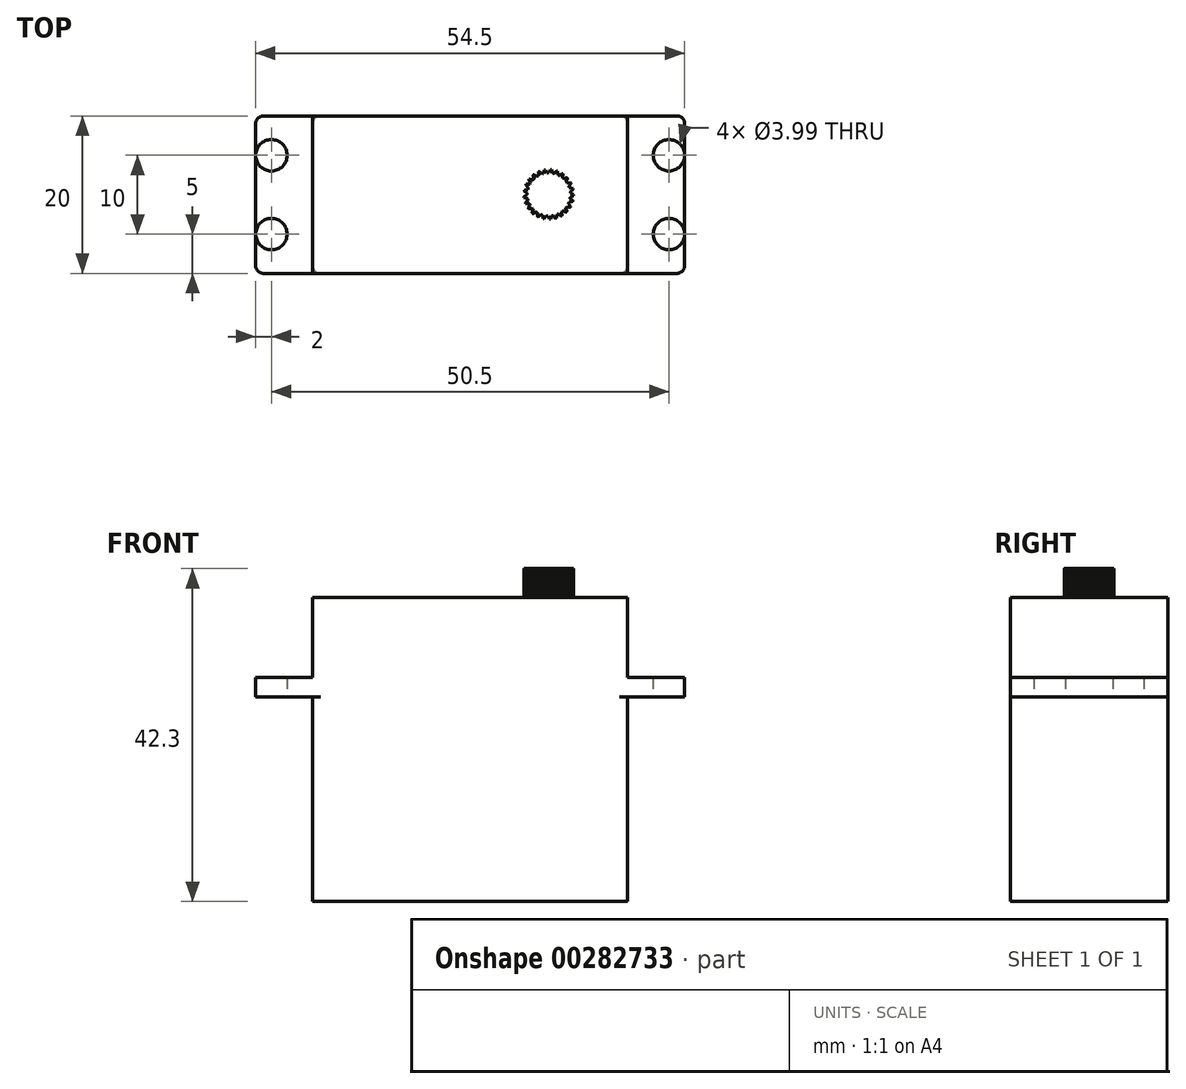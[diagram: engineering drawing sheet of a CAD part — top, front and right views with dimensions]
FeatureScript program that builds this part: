
annotation { "Feature Type Name" : "Feature", "Feature Type Description" : "" }
export const myFeature = defineFeature(function(context is Context, id is Id, definition is map)
    precondition{}
    {
        {
            var Q0;
            Q0=qCreatedBy(makeId("Top.planeOp"),FACE);
            var sketch = newSketch(context, id + "F0", { "sketchPlane" : qUnion([Q0])});
            skLineSegment(sketch, "E0", {"start": v(-74.17, 0) * mm, "end": v(76.51, 0) * mm, "construction": true});
            skLineSegment(sketch, "E1", {"start": v(0, 74.75) * mm, "end": v(0, -75.53) * mm, "construction": true});
            skLineSegment(sketch, "E2.bottom", {"start": v(19, -10) * mm, "end": v(-19, -10) * mm});
            skLineSegment(sketch, "E2.top", {"start": v(19, 10) * mm, "end": v(-19, 10) * mm});
            skLineSegment(sketch, "E2.left", {"start": v(20, -9) * mm, "end": v(20, 9) * mm});
            skLineSegment(sketch, "E2.right", {"start": v(-20, -9) * mm, "end": v(-20, 9) * mm});
            skPoint(sketch, "E2.middle", {"position": v(0, 0) * mm});
            skPoint(sketch, "E3.visualSharp", {"position": v(-20, 10) * mm});
            skArc(sketch, "E3.filletArc", {"start": v(-19, 10) * mm, "mid": v(-19.7, 9.7) * mm, "end": v(-20, 9) * mm});
            skPoint(sketch, "E4.visualSharp", {"position": v(20, 10) * mm});
            skArc(sketch, "E4.filletArc", {"start": v(20, 9) * mm, "mid": v(19.7, 9.7) * mm, "end": v(19, 10) * mm});
            skPoint(sketch, "E5.visualSharp", {"position": v(20, -10) * mm});
            skArc(sketch, "E5.filletArc", {"start": v(19, -10) * mm, "mid": v(19.7, -9.7) * mm, "end": v(20, -9) * mm});
            skPoint(sketch, "E6.visualSharp", {"position": v(-20, -10) * mm});
            skArc(sketch, "E6.filletArc", {"start": v(-20, -9) * mm, "mid": v(-19.7, -9.7) * mm, "end": v(-19, -10) * mm});
            skSolve(sketch);
        }
        {
            var Q0;
            Q0 = qSketchRegion(id + "F0", true);
            extrude(context, id + "F1", {"entities" : qUnion([Q0]), "depth" : 26 * mm});
        }
        {
            var Q0;
            Q0=makeQuery(id+"F1.opExtrude","CAP_FACE",FACE,{"disambiguationData":[OSD([sQuery(id+"F0.wireOp",EDGE,"E2.bottom"),sQuery(id+"F0.wireOp",EDGE,"E2.top"),sQuery(id+"F0.wireOp",EDGE,"E2.left"),sQuery(id+"F0.wireOp",EDGE,"E2.right"),sQuery(id+"F0.wireOp",EDGE,"E3.filletArc"),sQuery(id+"F0.wireOp",EDGE,"E4.filletArc"),sQuery(id+"F0.wireOp",EDGE,"E5.filletArc"),sQuery(id+"F0.wireOp",EDGE,"E6.filletArc")])],"isStart":false});
            var sketch = newSketch(context, id + "F2", { "sketchPlane" : qUnion([Q0])});
            skLineSegment(sketch, "E7", {"start": v(-69.92, 0) * mm, "end": v(54, 0) * mm, "construction": true});
            skPoint(sketch, "E7.startSnap0", {"position": v(-20, 0) * mm});
            skLineSegment(sketch, "E8", {"start": v(0, 31.92) * mm, "end": v(0, -23.22) * mm, "construction": true});
            skLineSegment(sketch, "E9.bottom", {"start": v(26.25, -10) * mm, "end": v(-26.25, -10) * mm});
            skLineSegment(sketch, "E9.top", {"start": v(26.25, 10) * mm, "end": v(-26.25, 10) * mm});
            skLineSegment(sketch, "E9.left", {"start": v(27.25, -9) * mm, "end": v(27.25, 9) * mm});
            skLineSegment(sketch, "E9.right", {"start": v(-27.25, -9) * mm, "end": v(-27.25, 9) * mm});
            skPoint(sketch, "E9.middle", {"position": v(0, 0) * mm});
            skLineSegment(sketch, "E10", {"start": v(-25.25, 12.88) * mm, "end": v(-25.25, -17.15) * mm, "construction": true});
            skPoint(sketch, "E11", {"position": v(-25.25, 5) * mm});
            skPoint(sketch, "E12", {"position": v(-25.25, -5) * mm});
            skPoint(sketch, "E13.MirrorP", {"position": v(25.25, 5) * mm});
            skPoint(sketch, "E14.MirrorP", {"position": v(25.25, -5) * mm});
            skPoint(sketch, "E15.visualSharp", {"position": v(-27.25, 10) * mm});
            skArc(sketch, "E15.filletArc", {"start": v(-26.25, 10) * mm, "mid": v(-26.96, 9.7) * mm, "end": v(-27.25, 9) * mm});
            skPoint(sketch, "E16.visualSharp", {"position": v(-27.25, -10) * mm});
            skArc(sketch, "E16.filletArc", {"start": v(-27.25, -9) * mm, "mid": v(-26.96, -9.7) * mm, "end": v(-26.25, -10) * mm});
            skPoint(sketch, "E17.visualSharp", {"position": v(27.25, 10) * mm});
            skArc(sketch, "E17.filletArc", {"start": v(27.25, 9) * mm, "mid": v(26.96, 9.7) * mm, "end": v(26.25, 10) * mm});
            skPoint(sketch, "E18.visualSharp", {"position": v(27.25, -10) * mm});
            skArc(sketch, "E18.filletArc", {"start": v(26.25, -10) * mm, "mid": v(26.96, -9.7) * mm, "end": v(27.25, -9) * mm});
            skSolve(sketch);
        }
        {
            var Q0;
            Q0 = qSketchRegion(id + "F2", true);
            extrude(context, id + "F3", {"entities" : qUnion([Q0]), "operationType" : NewBodyOperationType.ADD, "depth" : 2.5 * mm});
        }
        {
            var Q0;
            Q0=sQuery(id+"F2.wireOp",VERTEX,"E11");
            var Q1;
            Q1=sQuery(id+"F2.wireOp",VERTEX,"E12");
            var Q2;
            Q2=sQuery(id+"F2.wireOp",VERTEX,"E13.MirrorP");
            var Q3;
            Q3=sQuery(id+"F2.wireOp",VERTEX,"E14.MirrorP");
            var Q4;
            Q4=makeQuery(id+"F1.opExtrude","SWEPT_BODY",BODY,{"disambiguationData":[OSD([sQuery(id+"F0.wireOp",EDGE,"E2.bottom"),sQuery(id+"F0.wireOp",EDGE,"E2.top"),sQuery(id+"F0.wireOp",EDGE,"E2.left"),sQuery(id+"F0.wireOp",EDGE,"E2.right"),sQuery(id+"F0.wireOp",EDGE,"E3.filletArc"),sQuery(id+"F0.wireOp",EDGE,"E4.filletArc"),sQuery(id+"F0.wireOp",EDGE,"E5.filletArc"),sQuery(id+"F0.wireOp",EDGE,"E6.filletArc")])]});
            hole(context, id + "F4", {"style" : HoleStyle.SIMPLE, "endStyle" : HoleEndStyle.BLIND, "oppositeDirection" : true, "holeDiameter" : 4 * mm, "holeDepth" : 5 * mm, "tappedDepth" : 12 * mm, "tapClearance" : 3, "startFromSketch" : true, "locations" : qUnion([Q0, Q1, Q2, Q3]), "scope" : qUnion([Q4])});
        }
        {
            var Q0;
            Q0=makeQuery(id+"F3.opExtrude","CAP_FACE",FACE,{"disambiguationData":[OSD([sQuery(id+"F2.wireOp",EDGE,"E9.bottom"),sQuery(id+"F2.wireOp",EDGE,"E9.top"),sQuery(id+"F2.wireOp",EDGE,"E9.left"),sQuery(id+"F2.wireOp",EDGE,"E9.right"),sQuery(id+"F2.wireOp",EDGE,"E15.filletArc"),sQuery(id+"F2.wireOp",EDGE,"E16.filletArc"),sQuery(id+"F2.wireOp",EDGE,"E17.filletArc"),sQuery(id+"F2.wireOp",EDGE,"E18.filletArc")])],"isStart":false});
            var sketch = newSketch(context, id + "F5", { "sketchPlane" : qUnion([Q0])});
            skLineSegment(sketch, "E19.bottom", {"start": v(20, -10) * mm, "end": v(-20, -10) * mm});
            skLineSegment(sketch, "E19.top", {"start": v(20, 10) * mm, "end": v(-20, 10) * mm});
            skLineSegment(sketch, "E19.left", {"start": v(20, -10) * mm, "end": v(20, 10) * mm});
            skLineSegment(sketch, "E19.right", {"start": v(-20, -10) * mm, "end": v(-20, 10) * mm});
            skPoint(sketch, "E19.middle", {"position": v(0, 0) * mm});
            skSolve(sketch);
        }
        {
            var Q0;
            Q0 = qSketchRegion(id + "F5", true);
            extrude(context, id + "F6", {"entities" : qUnion([Q0]), "operationType" : NewBodyOperationType.ADD, "depth" : 10.1 * mm});
        }
        {
            var Q0;
            Q0=makeQuery(id+"F6.opExtrude","CAP_FACE",FACE,{"disambiguationData":[OSD([sQuery(id+"F5.wireOp",EDGE,"E19.bottom"),sQuery(id+"F5.wireOp",EDGE,"E19.top"),sQuery(id+"F5.wireOp",EDGE,"E19.left"),sQuery(id+"F5.wireOp",EDGE,"E19.right")])],"isStart":false});
            var sketch = newSketch(context, id + "F7", { "sketchPlane" : qUnion([Q0])});
            skLineSegment(sketch, "E20", {"start": v(-27.08, 0) * mm, "end": v(27.57, 0) * mm, "construction": true});
            skPoint(sketch, "E20.startSnap0", {"position": v(-20, 0) * mm});
            skPoint(sketch, "E20.endSnap0", {"position": v(20, 0) * mm});
            skLineSegment(sketch, "E21", {"start": v(0, 10) * mm, "end": v(0, -10) * mm, "construction": true});
            skLineSegment(sketch, "E22", {"start": v(10, 10) * mm, "end": v(10, -10) * mm, "construction": true});
            skPoint(sketch, "E23", {"position": v(10, 0) * mm});
            skCircle(sketch, "E24", {"center": v(10, 0) * mm, "radius": 2.5 * mm});
            skLineSegment(sketch, "E25", {"start": v(30, 0.07) * mm, "end": v(30, -0.07) * mm});
            skLineSegment(sketch, "E26", {"start": v(28.57, 1.57) * mm, "end": v(13.29, 2.34) * mm});
            skLineSegment(sketch, "E27", {"start": v(28.58, -1.57) * mm, "end": v(13.28, -2.34) * mm});
            skPoint(sketch, "E28.visualSharp", {"position": v(30, 1.5) * mm});
            skArc(sketch, "E28.filletArc", {"start": v(30, 0.07) * mm, "mid": v(29.59, 1.1) * mm, "end": v(28.57, 1.57) * mm});
            skPoint(sketch, "E29.visualSharp", {"position": v(30, -1.5) * mm});
            skArc(sketch, "E29.filletArc", {"start": v(28.58, -1.57) * mm, "mid": v(29.59, -1.1) * mm, "end": v(30, -0.07) * mm});
            skLineSegment(sketch, "E30.1.0", {"start": v(8.43, 18.57) * mm, "end": v(7.66, 3.29) * mm});
            skPoint(sketch, "E30.1.1", {"position": v(8.5, 20) * mm});
            skArc(sketch, "E30.1.2", {"start": v(9.93, 20) * mm, "mid": v(8.9, 19.59) * mm, "end": v(8.43, 18.57) * mm});
            skArc(sketch, "E30.1.3", {"start": v(11.57, 18.58) * mm, "mid": v(11.1, 19.59) * mm, "end": v(10.07, 20) * mm});
            skLineSegment(sketch, "E30.1.4", {"start": v(11.57, 18.58) * mm, "end": v(12.34, 3.28) * mm});
            skLineSegment(sketch, "E30.2.0", {"start": v(-8.57, -1.57) * mm, "end": v(6.71, -2.34) * mm});
            skPoint(sketch, "E30.2.1", {"position": v(-10, -1.5) * mm});
            skArc(sketch, "E30.2.2", {"start": v(-10, -0.07) * mm, "mid": v(-9.59, -1.1) * mm, "end": v(-8.57, -1.57) * mm});
            skArc(sketch, "E30.2.3", {"start": v(-8.58, 1.57) * mm, "mid": v(-9.59, 1.1) * mm, "end": v(-10, 0.07) * mm});
            skLineSegment(sketch, "E30.2.4", {"start": v(-8.58, 1.57) * mm, "end": v(6.72, 2.34) * mm});
            skLineSegment(sketch, "E30.3.0", {"start": v(11.57, -18.57) * mm, "end": v(12.34, -3.29) * mm});
            skPoint(sketch, "E30.3.1", {"position": v(11.5, -20) * mm});
            skArc(sketch, "E30.3.2", {"start": v(10.07, -20) * mm, "mid": v(11.1, -19.59) * mm, "end": v(11.57, -18.57) * mm});
            skArc(sketch, "E30.3.3", {"start": v(8.43, -18.58) * mm, "mid": v(8.9, -19.59) * mm, "end": v(9.93, -20) * mm});
            skLineSegment(sketch, "E30.3.4", {"start": v(8.43, -18.58) * mm, "end": v(7.66, -3.28) * mm});
            skPoint(sketch, "E31.newPointA", {"position": v(12.5, 0.13) * mm});
            skPoint(sketch, "E31.newPointB", {"position": v(10, 2.5) * mm});
            skArc(sketch, "E31.filletArc", {"start": v(12.34, 3.28) * mm, "mid": v(12.63, 2.63) * mm, "end": v(13.29, 2.34) * mm});
            skPoint(sketch, "E32.newPointA", {"position": v(12.5, 0) * mm});
            skPoint(sketch, "E32.newPointB", {"position": v(10.13, -2.5) * mm});
            skArc(sketch, "E32.filletArc", {"start": v(13.28, -2.34) * mm, "mid": v(12.63, -2.63) * mm, "end": v(12.34, -3.29) * mm});
            skPoint(sketch, "E33.newPointA", {"position": v(10, -2.5) * mm});
            skPoint(sketch, "E33.newPointB", {"position": v(7.5, -0.13) * mm});
            skArc(sketch, "E33.filletArc", {"start": v(7.66, -3.28) * mm, "mid": v(7.37, -2.63) * mm, "end": v(6.71, -2.34) * mm});
            skPoint(sketch, "E34.newPointA", {"position": v(9.87, 2.5) * mm});
            skPoint(sketch, "E34.newPointB", {"position": v(7.5, 0) * mm});
            skArc(sketch, "E34.filletArc", {"start": v(6.72, 2.34) * mm, "mid": v(7.37, 2.63) * mm, "end": v(7.66, 3.29) * mm});
            skSolve(sketch);
        }
        {
            var Q0;
            Q0 = qSketchRegion(id + "F7", true);
            extrude(context, id + "F8", {"entities" : qUnion([Q0]), "depth" : 6 * mm});
        }
        {
            var Q0;
            Q0=makeQuery(id+"F8.opExtrude","CAP_FACE",FACE,{"disambiguationData":[OSD([sQuery(id+"F7.wireOp",EDGE,"E24")])],"isStart":false});
            var sketch = newSketch(context, id + "F9", { "sketchPlane" : qUnion([Q0])});
            skLineSegment(sketch, "E35", {"start": v(-26.82, 0) * mm, "end": v(26.9, 0) * mm, "construction": true});
            skLineSegment(sketch, "E36", {"start": v(10, 9.8) * mm, "end": v(10, -10.05) * mm, "construction": true});
            skCircle(sketch, "E37", {"center": v(10, 0) * mm, "radius": 2.5 * mm, "construction": true});
            skLineSegment(sketch, "E38", {"start": v(-7, 0.09) * mm, "end": v(-7, -0.09) * mm});
            skLineSegment(sketch, "E39", {"start": v(-5.59, 1.58) * mm, "end": v(4.98, 2.2) * mm});
            skLineSegment(sketch, "E40", {"start": v(-5.59, -1.58) * mm, "end": v(4.97, -2.2) * mm});
            skPoint(sketch, "E41.visualSharp", {"position": v(-7, 1.5) * mm});
            skArc(sketch, "E41.filletArc", {"start": v(-5.59, 1.58) * mm, "mid": v(-6.6, 1.11) * mm, "end": v(-7, 0.09) * mm});
            skPoint(sketch, "E42.visualSharp", {"position": v(-7, -1.5) * mm});
            skArc(sketch, "E42.filletArc", {"start": v(-7, -0.09) * mm, "mid": v(-6.6, -1.11) * mm, "end": v(-5.59, -1.58) * mm});
            skLineSegment(sketch, "E43.1.0", {"start": v(8.42, -15.59) * mm, "end": v(7.8, -5.02) * mm});
            skArc(sketch, "E43.1.1", {"start": v(8.42, -15.59) * mm, "mid": v(8.89, -16.6) * mm, "end": v(9.91, -17) * mm});
            skArc(sketch, "E43.1.2", {"start": v(10.09, -17) * mm, "mid": v(11.11, -16.6) * mm, "end": v(11.58, -15.59) * mm});
            skLineSegment(sketch, "E43.1.3", {"start": v(11.58, -15.59) * mm, "end": v(12.2, -5.03) * mm});
            skLineSegment(sketch, "E43.1.4", {"start": v(9.91, -17) * mm, "end": v(10.09, -17) * mm});
            skLineSegment(sketch, "E43.2.0", {"start": v(25.59, -1.58) * mm, "end": v(15.02, -2.2) * mm});
            skArc(sketch, "E43.2.1", {"start": v(25.59, -1.58) * mm, "mid": v(26.6, -1.11) * mm, "end": v(27, -0.09) * mm});
            skArc(sketch, "E43.2.2", {"start": v(27, 0.09) * mm, "mid": v(26.6, 1.11) * mm, "end": v(25.59, 1.58) * mm});
            skLineSegment(sketch, "E43.2.3", {"start": v(25.59, 1.58) * mm, "end": v(15.03, 2.2) * mm});
            skLineSegment(sketch, "E43.2.4", {"start": v(27, -0.09) * mm, "end": v(27, 0.09) * mm});
            skLineSegment(sketch, "E43.3.0", {"start": v(11.58, 15.59) * mm, "end": v(12.2, 5.02) * mm});
            skArc(sketch, "E43.3.1", {"start": v(11.58, 15.59) * mm, "mid": v(11.11, 16.6) * mm, "end": v(10.09, 17) * mm});
            skArc(sketch, "E43.3.2", {"start": v(9.91, 17) * mm, "mid": v(8.89, 16.6) * mm, "end": v(8.42, 15.59) * mm});
            skLineSegment(sketch, "E43.3.3", {"start": v(8.42, 15.59) * mm, "end": v(7.8, 5.03) * mm});
            skLineSegment(sketch, "E43.3.4", {"start": v(10.09, 17) * mm, "end": v(9.91, 17) * mm});
            skPoint(sketch, "E44.newPointA", {"position": v(9.85, 2.5) * mm});
            skPoint(sketch, "E44.newPointB", {"position": v(7.5, 0) * mm});
            skArc(sketch, "E44.filletArc", {"start": v(4.98, 2.2) * mm, "mid": v(6.92, 3.08) * mm, "end": v(7.8, 5.03) * mm});
            skPoint(sketch, "E45.newPointA", {"position": v(12.5, 0.15) * mm});
            skPoint(sketch, "E45.newPointB", {"position": v(10, 2.5) * mm});
            skArc(sketch, "E45.filletArc", {"start": v(12.2, 5.02) * mm, "mid": v(13.08, 3.08) * mm, "end": v(15.03, 2.2) * mm});
            skPoint(sketch, "E46.newPointA", {"position": v(10.15, -2.5) * mm});
            skPoint(sketch, "E46.newPointB", {"position": v(12.5, 0) * mm});
            skArc(sketch, "E46.filletArc", {"start": v(15.02, -2.2) * mm, "mid": v(13.08, -3.08) * mm, "end": v(12.2, -5.03) * mm});
            skPoint(sketch, "E47.newPointA", {"position": v(10, -2.5) * mm});
            skPoint(sketch, "E47.newPointB", {"position": v(7.5, -0.15) * mm});
            skArc(sketch, "E47.filletArc", {"start": v(7.8, -5.02) * mm, "mid": v(6.92, -3.08) * mm, "end": v(4.97, -2.2) * mm});
            skSolve(sketch);
        }
        {
            var Q0;
            Q0 = qSketchRegion(id + "F9", true);
            extrude(context, id + "F10", {"entities" : qUnion([Q0]), "operationType" : NewBodyOperationType.ADD, "depth" : 2 * mm});
        }
        {
            var Q0;
            Q0=makeQuery(id+"F8.opExtrude","SWEPT_BODY",BODY,{"disambiguationData":[OSD([sQuery(id+"F7.wireOp",EDGE,"E24")])]});
            deleteBodies(context, id + "F11", {"entities" : qUnion([Q0])});
        }
        {
            var Q0;
            Q0=makeQuery(id+"F6.opExtrude","CAP_FACE",FACE,{"disambiguationData":[OSD([sQuery(id+"F5.wireOp",EDGE,"E19.bottom"),sQuery(id+"F5.wireOp",EDGE,"E19.top"),sQuery(id+"F5.wireOp",EDGE,"E19.left"),sQuery(id+"F5.wireOp",EDGE,"E19.right")])],"isStart":false});
            var sketch = newSketch(context, id + "F12", { "sketchPlane" : qUnion([Q0])});
            skLineSegment(sketch, "E48", {"start": v(-32.03, 0) * mm, "end": v(35.55, 0) * mm, "construction": true});
            skPoint(sketch, "E48.startSnap0", {"position": v(-20, 0) * mm});
            skPoint(sketch, "E48.endSnap0", {"position": v(20, 0) * mm});
            skLineSegment(sketch, "E49", {"start": v(10, 15) * mm, "end": v(10, -15) * mm, "construction": true});
            skPoint(sketch, "E50", {"position": v(10, 0) * mm});
            skCircle(sketch, "E51", {"center": v(10, 0.03) * mm, "radius": 2.75 * mm, "construction": true});
            skArc(sketch, "E52", {"start": v(10.2, 3.17) * mm, "mid": v(9.72, -3.11) * mm, "end": v(10.34, 3.16) * mm, "construction": true});
            skLineSegment(sketch, "E53", {"start": v(10, 0.03) * mm, "end": v(10.82, 3.22) * mm, "construction": true});
            skLineSegment(sketch, "E54", {"start": v(10, 0.03) * mm, "end": v(10.57, 3.28) * mm, "construction": true});
            skLineSegment(sketch, "E55", {"start": v(10, 0.03) * mm, "end": v(10.2, 3.18) * mm, "construction": true});
            skLineSegment(sketch, "E56", {"start": v(10, 0.03) * mm, "end": v(10.35, 3.3) * mm, "construction": true});
            skLineSegment(sketch, "E57", {"start": v(10, 2.78) * mm, "end": v(10.2, 3.17) * mm});
            skLineSegment(sketch, "E58", {"start": v(10.33, 3.16) * mm, "end": v(10.47, 2.73) * mm});
            skArc(sketch, "E59", {"start": v(10.2, 3.17) * mm, "mid": v(10.27, 3.16) * mm, "end": v(10.34, 3.16) * mm});
            skArc(sketch, "E60", {"start": v(10.47, 2.73) * mm, "mid": v(10.58, 2.71) * mm, "end": v(10.68, 2.7) * mm});
            skLineSegment(sketch, "E61.1.0", {"start": v(9.31, 2.7) * mm, "end": v(9.42, 3.12) * mm});
            skArc(sketch, "E61.1.1", {"start": v(9.42, 3.12) * mm, "mid": v(9.48, 3.13) * mm, "end": v(9.55, 3.14) * mm});
            skLineSegment(sketch, "E61.1.2", {"start": v(9.54, 3.15) * mm, "end": v(9.79, 2.77) * mm});
            skArc(sketch, "E61.1.3", {"start": v(9.79, 2.77) * mm, "mid": v(9.9, 2.77) * mm, "end": v(10, 2.78) * mm});
            skLineSegment(sketch, "E61.2.0", {"start": v(8.67, 2.44) * mm, "end": v(8.67, 2.88) * mm});
            skArc(sketch, "E61.2.1", {"start": v(8.67, 2.88) * mm, "mid": v(8.73, 2.9) * mm, "end": v(8.78, 2.94) * mm});
            skLineSegment(sketch, "E61.2.2", {"start": v(8.78, 2.94) * mm, "end": v(9.11, 2.63) * mm});
            skArc(sketch, "E61.2.3", {"start": v(9.11, 2.63) * mm, "mid": v(9.21, 2.66) * mm, "end": v(9.31, 2.7) * mm});
            skLineSegment(sketch, "E61.3.0", {"start": v(8.11, 2.03) * mm, "end": v(8, 2.46) * mm});
            skArc(sketch, "E61.3.1", {"start": v(8, 2.46) * mm, "mid": v(8.05, 2.5) * mm, "end": v(8.1, 2.54) * mm});
            skLineSegment(sketch, "E61.3.2", {"start": v(8.1, 2.54) * mm, "end": v(8.5, 2.33) * mm});
            skArc(sketch, "E61.3.3", {"start": v(8.5, 2.33) * mm, "mid": v(8.58, 2.38) * mm, "end": v(8.67, 2.44) * mm});
            skLineSegment(sketch, "E61.4.0", {"start": v(7.67, 1.5) * mm, "end": v(7.45, 1.89) * mm});
            skArc(sketch, "E61.4.1", {"start": v(7.45, 1.89) * mm, "mid": v(7.5, 1.94) * mm, "end": v(7.53, 2) * mm});
            skLineSegment(sketch, "E61.4.2", {"start": v(7.53, 2) * mm, "end": v(7.97, 1.88) * mm});
            skArc(sketch, "E61.4.3", {"start": v(7.97, 1.88) * mm, "mid": v(8.04, 1.96) * mm, "end": v(8.11, 2.03) * mm});
            skLineSegment(sketch, "E61.5.0", {"start": v(7.38, 0.88) * mm, "end": v(7.07, 1.2) * mm});
            skArc(sketch, "E61.5.1", {"start": v(7.07, 1.2) * mm, "mid": v(7.1, 1.26) * mm, "end": v(7.12, 1.32) * mm});
            skLineSegment(sketch, "E61.5.2", {"start": v(7.12, 1.32) * mm, "end": v(7.57, 1.32) * mm});
            skArc(sketch, "E61.5.3", {"start": v(7.57, 1.32) * mm, "mid": v(7.62, 1.41) * mm, "end": v(7.67, 1.5) * mm});
            skLineSegment(sketch, "E61.6.0", {"start": v(7.25, 0.2) * mm, "end": v(6.87, 0.44) * mm});
            skArc(sketch, "E61.6.1", {"start": v(6.87, 0.44) * mm, "mid": v(6.88, 0.5) * mm, "end": v(6.9, 0.56) * mm});
            skLineSegment(sketch, "E61.6.2", {"start": v(6.89, 0.56) * mm, "end": v(7.32, 0.68) * mm});
            skArc(sketch, "E61.6.3", {"start": v(7.32, 0.68) * mm, "mid": v(7.35, 0.78) * mm, "end": v(7.38, 0.88) * mm});
            skLineSegment(sketch, "E61.7.0", {"start": v(7.3, -0.49) * mm, "end": v(6.87, -0.35) * mm});
            skArc(sketch, "E61.7.1", {"start": v(6.87, -0.35) * mm, "mid": v(6.86, -0.29) * mm, "end": v(6.85, -0.23) * mm});
            skLineSegment(sketch, "E61.7.2", {"start": v(6.85, -0.23) * mm, "end": v(7.25, 0) * mm});
            skArc(sketch, "E61.7.3", {"start": v(7.25, 0) * mm, "mid": v(7.25, 0.1) * mm, "end": v(7.25, 0.2) * mm});
            skLineSegment(sketch, "E61.8.0", {"start": v(7.5, -1.14) * mm, "end": v(7.06, -1.12) * mm});
            skArc(sketch, "E61.8.1", {"start": v(7.06, -1.12) * mm, "mid": v(7.04, -1.06) * mm, "end": v(7.02, -1) * mm});
            skLineSegment(sketch, "E61.8.2", {"start": v(7.01, -1) * mm, "end": v(7.34, -0.7) * mm});
            skArc(sketch, "E61.8.3", {"start": v(7.34, -0.7) * mm, "mid": v(7.31, -0.6) * mm, "end": v(7.3, -0.49) * mm});
            skLineSegment(sketch, "E61.9.0", {"start": v(7.88, -1.73) * mm, "end": v(7.44, -1.81) * mm});
            skArc(sketch, "E61.9.1", {"start": v(7.44, -1.81) * mm, "mid": v(7.4, -1.76) * mm, "end": v(7.36, -1.7) * mm});
            skLineSegment(sketch, "E61.9.2", {"start": v(7.36, -1.7) * mm, "end": v(7.6, -1.33) * mm});
            skArc(sketch, "E61.9.3", {"start": v(7.6, -1.33) * mm, "mid": v(7.55, -1.24) * mm, "end": v(7.5, -1.14) * mm});
            skLineSegment(sketch, "E61.10.0", {"start": v(8.38, -2.2) * mm, "end": v(7.98, -2.4) * mm});
            skArc(sketch, "E61.10.1", {"start": v(7.98, -2.4) * mm, "mid": v(7.93, -2.35) * mm, "end": v(7.88, -2.3) * mm});
            skLineSegment(sketch, "E61.10.2", {"start": v(7.88, -2.3) * mm, "end": v(8.01, -1.88) * mm});
            skArc(sketch, "E61.10.3", {"start": v(8.01, -1.88) * mm, "mid": v(7.94, -1.8) * mm, "end": v(7.88, -1.73) * mm});
            skLineSegment(sketch, "E61.11.0", {"start": v(8.98, -2.53) * mm, "end": v(8.64, -2.82) * mm});
            skArc(sketch, "E61.11.1", {"start": v(8.64, -2.82) * mm, "mid": v(8.58, -2.79) * mm, "end": v(8.53, -2.76) * mm});
            skLineSegment(sketch, "E61.11.2", {"start": v(8.52, -2.76) * mm, "end": v(8.55, -2.31) * mm});
            skArc(sketch, "E61.11.3", {"start": v(8.55, -2.31) * mm, "mid": v(8.46, -2.26) * mm, "end": v(8.38, -2.2) * mm});
            skLineSegment(sketch, "E61.12.0", {"start": v(9.65, -2.7) * mm, "end": v(9.4, -3.06) * mm});
            skArc(sketch, "E61.12.1", {"start": v(9.4, -3.06) * mm, "mid": v(9.33, -3.05) * mm, "end": v(9.26, -3.04) * mm});
            skLineSegment(sketch, "E61.12.2", {"start": v(9.26, -3.04) * mm, "end": v(9.18, -2.6) * mm});
            skArc(sketch, "E61.12.3", {"start": v(9.18, -2.6) * mm, "mid": v(9.08, -2.57) * mm, "end": v(8.98, -2.53) * mm});
            skLineSegment(sketch, "E61.13.0", {"start": v(10.34, -2.7) * mm, "end": v(10.18, -3.12) * mm});
            skArc(sketch, "E61.13.1", {"start": v(10.18, -3.12) * mm, "mid": v(10.11, -3.12) * mm, "end": v(10.05, -3.12) * mm});
            skLineSegment(sketch, "E61.13.2", {"start": v(10.05, -3.13) * mm, "end": v(9.86, -2.72) * mm});
            skArc(sketch, "E61.13.3", {"start": v(9.86, -2.72) * mm, "mid": v(9.75, -2.71) * mm, "end": v(9.65, -2.7) * mm});
            skLineSegment(sketch, "E61.14.0", {"start": v(11, -2.53) * mm, "end": v(10.95, -2.97) * mm});
            skArc(sketch, "E61.14.1", {"start": v(10.95, -2.97) * mm, "mid": v(10.9, -3) * mm, "end": v(10.83, -3.01) * mm});
            skLineSegment(sketch, "E61.14.2", {"start": v(10.83, -3.01) * mm, "end": v(10.55, -2.67) * mm});
            skArc(sketch, "E61.14.3", {"start": v(10.55, -2.67) * mm, "mid": v(10.44, -2.69) * mm, "end": v(10.34, -2.7) * mm});
            skLineSegment(sketch, "E61.15.0", {"start": v(11.61, -2.2) * mm, "end": v(11.67, -2.64) * mm});
            skArc(sketch, "E61.15.1", {"start": v(11.67, -2.64) * mm, "mid": v(11.62, -2.67) * mm, "end": v(11.56, -2.7) * mm});
            skLineSegment(sketch, "E61.15.2", {"start": v(11.56, -2.7) * mm, "end": v(11.2, -2.45) * mm});
            skArc(sketch, "E61.15.3", {"start": v(11.2, -2.45) * mm, "mid": v(11.1, -2.49) * mm, "end": v(11, -2.53) * mm});
            skLineSegment(sketch, "E61.16.0", {"start": v(12.11, -1.73) * mm, "end": v(12.28, -2.14) * mm});
            skArc(sketch, "E61.16.1", {"start": v(12.28, -2.14) * mm, "mid": v(12.24, -2.19) * mm, "end": v(12.2, -2.23) * mm});
            skLineSegment(sketch, "E61.16.2", {"start": v(12.2, -2.23) * mm, "end": v(11.78, -2.07) * mm});
            skArc(sketch, "E61.16.3", {"start": v(11.78, -2.07) * mm, "mid": v(11.7, -2.14) * mm, "end": v(11.61, -2.2) * mm});
            skLineSegment(sketch, "E61.17.0", {"start": v(12.48, -1.14) * mm, "end": v(12.75, -1.5) * mm});
            skArc(sketch, "E61.17.1", {"start": v(12.75, -1.5) * mm, "mid": v(12.72, -1.56) * mm, "end": v(12.68, -1.62) * mm});
            skLineSegment(sketch, "E61.17.2", {"start": v(12.69, -1.62) * mm, "end": v(12.24, -1.56) * mm});
            skArc(sketch, "E61.17.3", {"start": v(12.24, -1.56) * mm, "mid": v(12.18, -1.64) * mm, "end": v(12.11, -1.73) * mm});
            skLineSegment(sketch, "E61.18.0", {"start": v(12.7, -0.49) * mm, "end": v(13.04, -0.77) * mm});
            skArc(sketch, "E61.18.1", {"start": v(13.04, -0.77) * mm, "mid": v(13.03, -0.83) * mm, "end": v(13, -0.9) * mm});
            skLineSegment(sketch, "E61.18.2", {"start": v(13, -0.9) * mm, "end": v(12.56, -0.95) * mm});
            skArc(sketch, "E61.18.3", {"start": v(12.56, -0.95) * mm, "mid": v(12.53, -1.05) * mm, "end": v(12.48, -1.14) * mm});
            skLineSegment(sketch, "E61.19.0", {"start": v(12.74, 0.2) * mm, "end": v(13.14, 0.01) * mm});
            skArc(sketch, "E61.19.1", {"start": v(13.14, 0.01) * mm, "mid": v(13.14, -0.05) * mm, "end": v(13.14, -0.12) * mm});
            skLineSegment(sketch, "E61.19.2", {"start": v(13.14, -0.12) * mm, "end": v(12.73, -0.28) * mm});
            skArc(sketch, "E61.19.3", {"start": v(12.73, -0.28) * mm, "mid": v(12.71, -0.39) * mm, "end": v(12.7, -0.49) * mm});
            skLineSegment(sketch, "E61.20.0", {"start": v(12.61, 0.88) * mm, "end": v(13.05, 0.8) * mm});
            skArc(sketch, "E61.20.1", {"start": v(13.05, 0.8) * mm, "mid": v(13.06, 0.73) * mm, "end": v(13.08, 0.67) * mm});
            skLineSegment(sketch, "E61.20.2", {"start": v(13.08, 0.67) * mm, "end": v(12.72, 0.4) * mm});
            skArc(sketch, "E61.20.3", {"start": v(12.72, 0.4) * mm, "mid": v(12.73, 0.3) * mm, "end": v(12.74, 0.2) * mm});
            skLineSegment(sketch, "E61.21.0", {"start": v(12.32, 1.5) * mm, "end": v(12.76, 1.53) * mm});
            skArc(sketch, "E61.21.1", {"start": v(12.76, 1.53) * mm, "mid": v(12.8, 1.47) * mm, "end": v(12.82, 1.42) * mm});
            skLineSegment(sketch, "E61.21.2", {"start": v(12.82, 1.42) * mm, "end": v(12.54, 1.07) * mm});
            skArc(sketch, "E61.21.3", {"start": v(12.54, 1.07) * mm, "mid": v(12.58, 0.98) * mm, "end": v(12.61, 0.88) * mm});
            skLineSegment(sketch, "E61.22.0", {"start": v(11.88, 2.03) * mm, "end": v(12.3, 2.17) * mm});
            skArc(sketch, "E61.22.1", {"start": v(12.3, 2.17) * mm, "mid": v(12.34, 2.12) * mm, "end": v(12.39, 2.08) * mm});
            skLineSegment(sketch, "E61.22.2", {"start": v(12.39, 2.08) * mm, "end": v(12.2, 1.67) * mm});
            skArc(sketch, "E61.22.3", {"start": v(12.2, 1.67) * mm, "mid": v(12.26, 1.59) * mm, "end": v(12.32, 1.5) * mm});
            skLineSegment(sketch, "E61.23.0", {"start": v(11.32, 2.44) * mm, "end": v(11.7, 2.68) * mm});
            skArc(sketch, "E61.23.1", {"start": v(11.7, 2.68) * mm, "mid": v(11.75, 2.64) * mm, "end": v(11.8, 2.6) * mm});
            skLineSegment(sketch, "E61.23.2", {"start": v(11.8, 2.6) * mm, "end": v(11.72, 2.17) * mm});
            skArc(sketch, "E61.23.3", {"start": v(11.72, 2.17) * mm, "mid": v(11.8, 2.1) * mm, "end": v(11.88, 2.03) * mm});
            skLineSegment(sketch, "E61.24.0", {"start": v(10.68, 2.7) * mm, "end": v(10.98, 3.02) * mm});
            skArc(sketch, "E61.24.1", {"start": v(10.98, 3.02) * mm, "mid": v(11.04, 3) * mm, "end": v(11.1, 2.97) * mm});
            skLineSegment(sketch, "E61.24.2", {"start": v(11.1, 2.98) * mm, "end": v(11.13, 2.53) * mm});
            skArc(sketch, "E61.24.3", {"start": v(11.13, 2.53) * mm, "mid": v(11.23, 2.49) * mm, "end": v(11.32, 2.44) * mm});
            skSolve(sketch);
        }
        {
            var Q0;
            Q0=makeQuery(id+"F12.imprint","IMPRINT",FACE,{"disambiguationData":[TD([[makeQuery(id+"F12.imprint","IMPRINT",EDGE,{"derivedFrom":sQuery(id+"F12.wireOp",EDGE,"E57")}),-1.0]])]});
            extrude(context, id + "F13", {"entities" : qUnion([Q0]), "depth" : 3.7 * mm});
        }
    });
